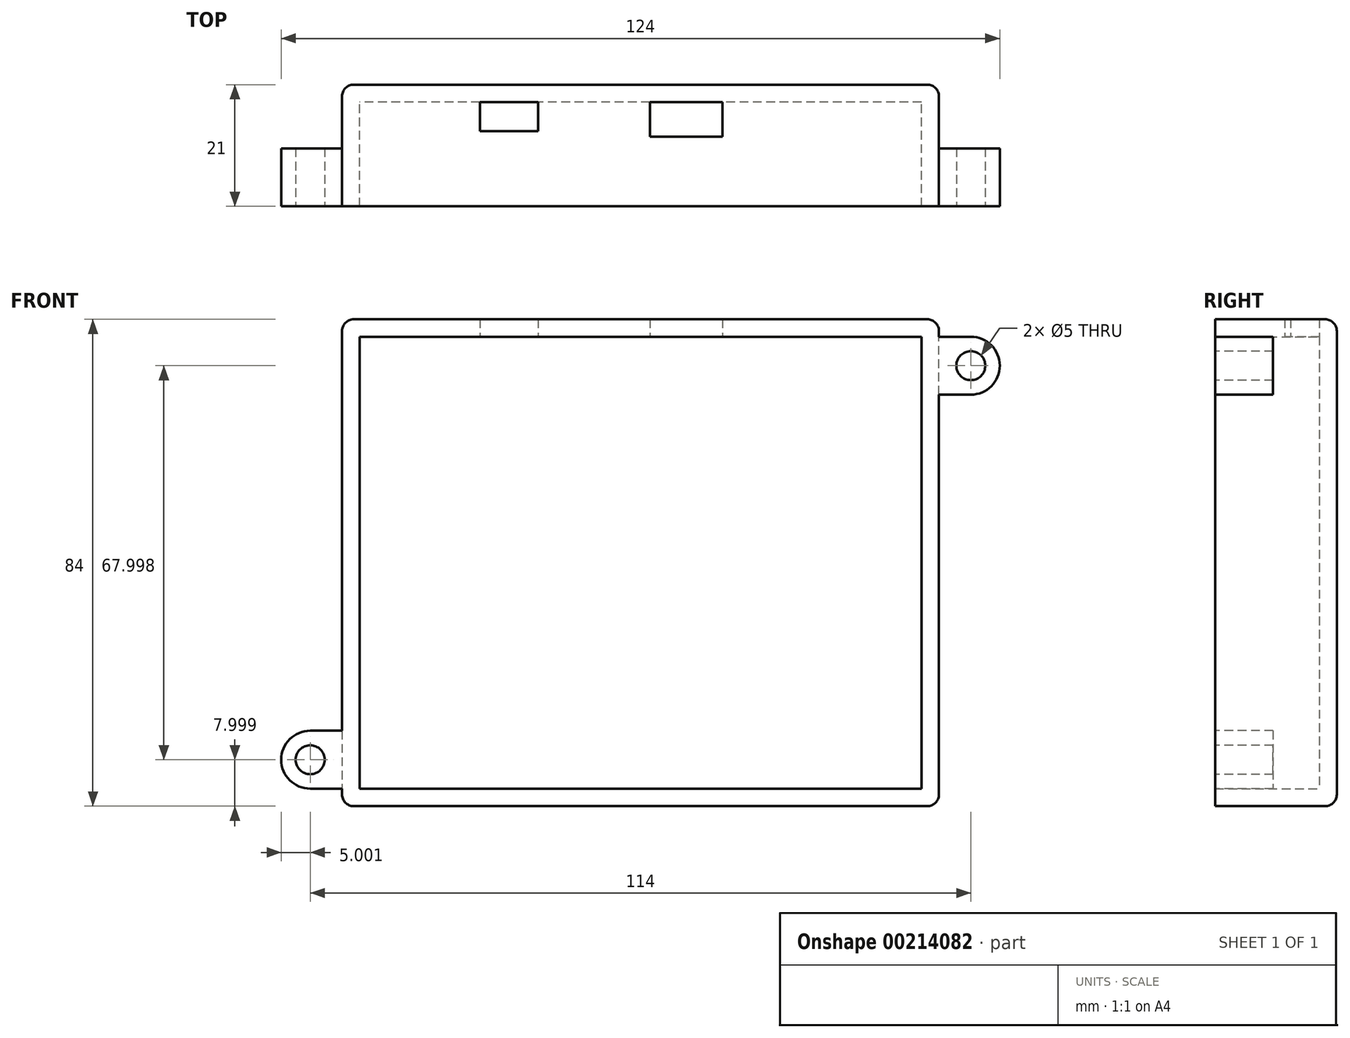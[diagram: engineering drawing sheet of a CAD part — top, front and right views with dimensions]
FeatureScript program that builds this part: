
annotation { "Feature Type Name" : "Feature", "Feature Type Description" : "" }
export const myFeature = defineFeature(function(context is Context, id is Id, definition is map)
    precondition{}
    {
        {
            var Q0;
            Q0=qCreatedBy(makeId("Front.planeOp"),FACE);
            var sketch = newSketch(context, id + "F0", { "sketchPlane" : qUnion([Q0])});
            skLineSegment(sketch, "E0", {"start": v(-34.86, 31.43) * mm, "end": v(-34.86, -46.57) * mm});
            skLineSegment(sketch, "E1", {"start": v(-34.86, -46.57) * mm, "end": v(62.14, -46.57) * mm});
            skLineSegment(sketch, "E2", {"start": v(62.14, -46.57) * mm, "end": v(62.14, 31.43) * mm});
            skLineSegment(sketch, "E3", {"start": v(62.14, 31.43) * mm, "end": v(-34.86, 31.43) * mm});
            skLineSegment(sketch, "E4", {"start": v(-37.86, 31.43) * mm, "end": v(-37.86, -46.57) * mm});
            skLineSegment(sketch, "E5", {"start": v(-37.86, -46.57) * mm, "end": v(-34.86, -46.57) * mm});
            skLineSegment(sketch, "E6", {"start": v(-37.86, 31.43) * mm, "end": v(-34.86, 31.43) * mm});
            skLineSegment(sketch, "E7", {"start": v(62.14, -46.57) * mm, "end": v(65.14, -46.57) * mm});
            skLineSegment(sketch, "E8", {"start": v(65.14, -46.57) * mm, "end": v(65.14, 31.43) * mm});
            skLineSegment(sketch, "E9", {"start": v(65.14, 31.43) * mm, "end": v(62.14, 31.43) * mm});
            skLineSegment(sketch, "E10", {"start": v(-37.86, 31.43) * mm, "end": v(-37.86, 34.43) * mm});
            skLineSegment(sketch, "E11", {"start": v(-37.86, 34.43) * mm, "end": v(65.14, 34.43) * mm});
            skLineSegment(sketch, "E12", {"start": v(65.14, 34.43) * mm, "end": v(65.14, 31.43) * mm});
            skLineSegment(sketch, "E13", {"start": v(-37.86, -46.57) * mm, "end": v(-37.86, -49.57) * mm});
            skLineSegment(sketch, "E14", {"start": v(-37.86, -49.57) * mm, "end": v(65.14, -49.57) * mm});
            skLineSegment(sketch, "E15", {"start": v(65.14, -49.57) * mm, "end": v(65.14, -46.57) * mm});
            skSolve(sketch);
        }
        {
            var Q0;
            Q0 = qSketchRegion(id + "F0", true);
            extrude(context, id + "F1", {"entities" : qUnion([Q0]), "depth" : 21 * mm});
        }
        {
            var Q0;
            Q0=makeQuery(id+"F1.opExtrude","SWEPT_EDGE",EDGE,{"disambiguationData":[OSD([sQuery(id+"F0.wireOp",EDGE,"E13"),sQuery(id+"F0.wireOp",EDGE,"E14")])]});
            var Q1;
            Q1=makeQuery(id+"F1.opExtrude","SWEPT_EDGE",EDGE,{"disambiguationData":[OSD([sQuery(id+"F0.wireOp",EDGE,"E14"),sQuery(id+"F0.wireOp",EDGE,"E15")])]});
            var Q2;
            Q2=makeQuery(id+"F1.opExtrude","CAP_EDGE",EDGE,{"disambiguationData":[OSD([sQuery(id+"F0.wireOp",EDGE,"E14")])],"isStart":true});
            var Q3;
            Q3=makeQuery(id+"F1.opExtrude","CAP_EDGE",EDGE,{"disambiguationData":[OSD([sQuery(id+"F0.wireOp",EDGE,"E4"),sQuery(id+"F0.wireOp",EDGE,"E10"),sQuery(id+"F0.wireOp",EDGE,"E13")])],"isStart":true});
            var Q4;
            Q4=makeQuery(id+"F1.opExtrude","SWEPT_EDGE",EDGE,{"disambiguationData":[OSD([sQuery(id+"F0.wireOp",EDGE,"E10"),sQuery(id+"F0.wireOp",EDGE,"E11")])]});
            var Q5;
            Q5=makeQuery(id+"F1.opExtrude","CAP_EDGE",EDGE,{"disambiguationData":[OSD([sQuery(id+"F0.wireOp",EDGE,"E11")])],"isStart":true});
            var Q6;
            Q6=makeQuery(id+"F1.opExtrude","SWEPT_EDGE",EDGE,{"disambiguationData":[OSD([sQuery(id+"F0.wireOp",EDGE,"E11"),sQuery(id+"F0.wireOp",EDGE,"E12")])]});
            var Q7;
            Q7=makeQuery(id+"F1.opExtrude","CAP_EDGE",EDGE,{"disambiguationData":[OSD([sQuery(id+"F0.wireOp",EDGE,"E8"),sQuery(id+"F0.wireOp",EDGE,"E12"),sQuery(id+"F0.wireOp",EDGE,"E15")])],"isStart":true});
            fillet(context, id + "F2", {"entities" : qUnion([Q0, Q1, Q2, Q3, Q4, Q5, Q6, Q7]), "radius" : 2 * mm, "tangentPropagation" : true, "allowEdgeOverflow" : false});
        }
        {
            var Q0;
            Q0=makeQuery(id+"F0.imprint","IMPRINT",FACE,{"disambiguationData":[TD([[makeQuery(id+"F0.imprint","IMPRINT",EDGE,{"derivedFrom":sQuery(id+"F0.wireOp",EDGE,"E0")}),1.0]])]});
            extrude(context, id + "F3", {"entities" : qUnion([Q0]), "operationType" : NewBodyOperationType.ADD, "depth" : 3 * mm});
        }
        {
            var Q0;
            Q0=makeQuery(id+"F1.opExtrude","SWEPT_FACE",FACE,{"disambiguationData":[OSD([sQuery(id+"F0.wireOp",EDGE,"E3")])]});
            var sketch = newSketch(context, id + "F4", { "sketchPlane" : qUnion([Q0])});
            skLineSegment(sketch, "E16", {"start": v(-14.05, 3) * mm, "end": v(-14.05, 8) * mm});
            skLineSegment(sketch, "E17", {"start": v(-14.05, 8) * mm, "end": v(-4.05, 8) * mm});
            skLineSegment(sketch, "E18", {"start": v(-4.05, 8) * mm, "end": v(-4.05, 3) * mm});
            skLineSegment(sketch, "E19", {"start": v(-4.05, 3) * mm, "end": v(-14.05, 3) * mm});
            skLineSegment(sketch, "E20", {"start": v(15.27, 3) * mm, "end": v(27.77, 3) * mm});
            skLineSegment(sketch, "E21", {"start": v(27.77, 3) * mm, "end": v(27.77, 9) * mm});
            skLineSegment(sketch, "E22", {"start": v(27.77, 9) * mm, "end": v(15.27, 9) * mm});
            skLineSegment(sketch, "E23", {"start": v(15.27, 9) * mm, "end": v(15.27, 3) * mm});
            skSolve(sketch);
        }
        {
            var Q0;
            Q0=makeQuery(id+"F4.imprint","IMPRINT",FACE,{"disambiguationData":[TD([[makeQuery(id+"F4.imprint","IMPRINT",EDGE,{"derivedFrom":sQuery(id+"F4.wireOp",EDGE,"E16")}),-1.0]])]});
            extrude(context, id + "F5", {"entities" : qUnion([Q0]), "operationType" : NewBodyOperationType.REMOVE, "oppositeDirection" : true, "depth" : 3 * mm});
        }
        {
            var Q0;
            Q0=makeQuery(id+"F1.opExtrude","CAP_FACE",FACE,{"disambiguationData":[OSD([sQuery(id+"F0.wireOp",EDGE,"E0"),sQuery(id+"F0.wireOp",EDGE,"E1"),sQuery(id+"F0.wireOp",EDGE,"E2"),sQuery(id+"F0.wireOp",EDGE,"E3"),sQuery(id+"F0.wireOp",EDGE,"E4"),sQuery(id+"F0.wireOp",EDGE,"E8"),sQuery(id+"F0.wireOp",EDGE,"E10"),sQuery(id+"F0.wireOp",EDGE,"E11"),sQuery(id+"F0.wireOp",EDGE,"E12"),sQuery(id+"F0.wireOp",EDGE,"E13"),sQuery(id+"F0.wireOp",EDGE,"E14"),sQuery(id+"F0.wireOp",EDGE,"E15")])],"isStart":false});
            var sketch = newSketch(context, id + "F6", { "sketchPlane" : qUnion([Q0])});
            skLineSegment(sketch, "E24", {"start": v(65.14, 31.43) * mm, "end": v(70.64, 31.43) * mm});
            skLineSegment(sketch, "E25", {"start": v(65.14, 21.43) * mm, "end": v(70.64, 21.43) * mm});
            skLineSegment(sketch, "E26", {"start": v(65.14, 31.43) * mm, "end": v(65.14, 21.43) * mm});
            skArc(sketch, "E27", {"start": v(70.64, 31.43) * mm, "mid": v(75.64, 26.43) * mm, "end": v(70.64, 21.43) * mm});
            skCircle(sketch, "E28", {"center": v(70.64, 26.43) * mm, "radius": 2.5 * mm});
            skLineSegment(sketch, "E29", {"start": v(-37.86, -46.57) * mm, "end": v(-43.36, -46.57) * mm});
            skLineSegment(sketch, "E30", {"start": v(-37.86, -46.57) * mm, "end": v(-37.86, -36.57) * mm});
            skLineSegment(sketch, "E31", {"start": v(-37.86, -36.57) * mm, "end": v(-43.36, -36.57) * mm});
            skArc(sketch, "E32", {"start": v(-43.36, -36.57) * mm, "mid": v(-48.36, -41.57) * mm, "end": v(-43.36, -46.57) * mm});
            skCircle(sketch, "E33", {"center": v(-43.36, -41.57) * mm, "radius": 2.5 * mm});
            skSolve(sketch);
        }
        {
            var Q0;
            Q0 = qSketchRegion(id + "F6", true);
            extrude(context, id + "F7", {"entities" : qUnion([Q0]), "operationType" : NewBodyOperationType.ADD, "oppositeDirection" : true, "depth" : 10 * mm});
        }
        {
            var Q0;
            Q0=makeQuery(id+"F4.imprint","IMPRINT",FACE,{"disambiguationData":[TD([[makeQuery(id+"F4.imprint","IMPRINT",EDGE,{"derivedFrom":sQuery(id+"F4.wireOp",EDGE,"E20")}),-1.0]])]});
            extrude(context, id + "F8", {"entities" : qUnion([Q0]), "operationType" : NewBodyOperationType.REMOVE, "oppositeDirection" : true, "depth" : 3 * mm});
        }
    });
